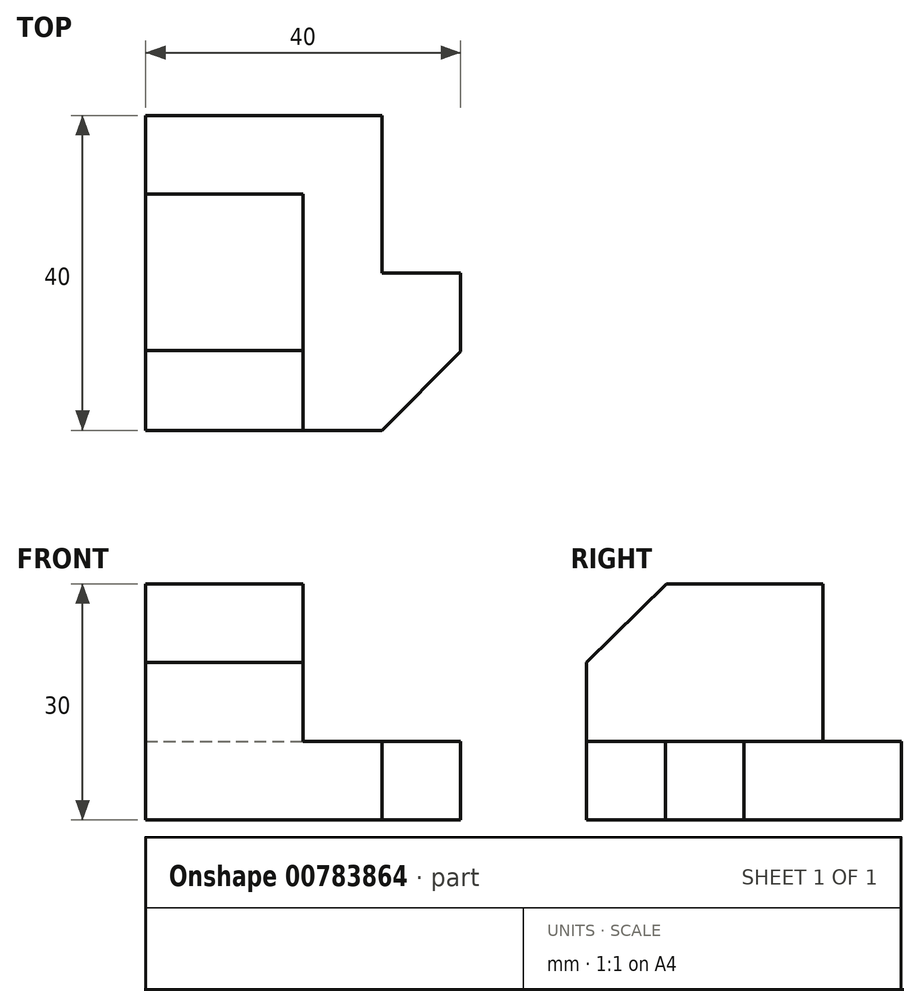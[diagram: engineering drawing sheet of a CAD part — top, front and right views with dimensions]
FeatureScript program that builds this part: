
annotation { "Feature Type Name" : "Feature", "Feature Type Description" : "" }
export const myFeature = defineFeature(function(context is Context, id is Id, definition is map)
    precondition{}
    {
        {
            var Q0;
            Q0=qCreatedBy(makeId("Top.planeOp"),FACE);
            var sketch = newSketch(context, id + "F0", { "sketchPlane" : qUnion([Q0])});
            skLineSegment(sketch, "E0.bottom", {"start": v(0, 0) * mm, "end": v(40, 0) * mm});
            skLineSegment(sketch, "E0.top", {"start": v(0, 40) * mm, "end": v(40, 40) * mm});
            skLineSegment(sketch, "E0.left", {"start": v(0, 0) * mm, "end": v(0, 40) * mm});
            skLineSegment(sketch, "E0.right", {"start": v(40, 0) * mm, "end": v(40, 40) * mm});
            skSolve(sketch);
        }
        {
            var Q0;
            Q0=makeQuery(id+"F0.imprint","IMPRINT",FACE,{"disambiguationData":[TD([[makeQuery(id+"F0.imprint","IMPRINT",EDGE,{"derivedFrom":sQuery(id+"F0.wireOp",EDGE,"E0.bottom")}),1.0]])]});
            extrude(context, id + "F1", {"entities" : qUnion([Q0]), "depth" : 30 * mm, "offsetDistance" : 25 * mm});
        }
        {
            var Q0;
            Q0=makeQuery(id+"F1.opExtrude","CAP_FACE",FACE,{"disambiguationData":[OSD([sQuery(id+"F0.wireOp",EDGE,"E0.bottom"),sQuery(id+"F0.wireOp",EDGE,"E0.top"),sQuery(id+"F0.wireOp",EDGE,"E0.left"),sQuery(id+"F0.wireOp",EDGE,"E0.right")])],"isStart":false});
            var sketch = newSketch(context, id + "F2", { "sketchPlane" : qUnion([Q0])});
            skLineSegment(sketch, "E1.bottom", {"start": v(40, 40) * mm, "end": v(30, 40) * mm});
            skLineSegment(sketch, "E1.top", {"start": v(40, 20) * mm, "end": v(30, 20) * mm});
            skLineSegment(sketch, "E1.left", {"start": v(40, 40) * mm, "end": v(40, 20) * mm});
            skLineSegment(sketch, "E1.right", {"start": v(30, 40) * mm, "end": v(30, 20) * mm});
            skSolve(sketch);
        }
        {
            var Q0;
            Q0=makeQuery(id+"F2.imprint","IMPRINT",FACE,{"disambiguationData":[TD([[makeQuery(id+"F2.imprint","IMPRINT",EDGE,{"derivedFrom":sQuery(id+"F2.wireOp",EDGE,"E1.bottom")}),-1.0]])]});
            extrude(context, id + "F3", {"entities" : qUnion([Q0]), "operationType" : NewBodyOperationType.REMOVE, "oppositeDirection" : true, "depth" : 30 * mm, "offsetDistance" : 25 * mm});
        }
        {
            var Q0;
            Q0=makeQuery(id+"F1.opExtrude","CAP_FACE",FACE,{"disambiguationData":[OSD([sQuery(id+"F0.wireOp",EDGE,"E0.bottom"),sQuery(id+"F0.wireOp",EDGE,"E0.top"),sQuery(id+"F0.wireOp",EDGE,"E0.left"),sQuery(id+"F0.wireOp",EDGE,"E0.right")])],"isStart":false});
            var sketch = newSketch(context, id + "F4", { "sketchPlane" : qUnion([Q0])});
            skLineSegment(sketch, "E2", {"start": v(0, 40) * mm, "end": v(0, 30) * mm});
            skLineSegment(sketch, "E3", {"start": v(0, 30) * mm, "end": v(20, 30) * mm});
            skLineSegment(sketch, "E4", {"start": v(20, 30) * mm, "end": v(20, 0) * mm});
            skLineSegment(sketch, "E5", {"start": v(20, 0) * mm, "end": v(40, 0) * mm});
            skLineSegment(sketch, "E6", {"start": v(40, 0) * mm, "end": v(40, 20) * mm});
            skLineSegment(sketch, "E7", {"start": v(40, 20) * mm, "end": v(30, 20) * mm});
            skLineSegment(sketch, "E8", {"start": v(30, 20) * mm, "end": v(30, 40) * mm});
            skLineSegment(sketch, "E9", {"start": v(30, 40) * mm, "end": v(0, 40) * mm});
            skSolve(sketch);
        }
        {
            var Q0;
            Q0=makeQuery(id+"F4.imprint","IMPRINT",FACE,{"disambiguationData":[TD([[makeQuery(id+"F4.imprint","IMPRINT",EDGE,{"derivedFrom":sQuery(id+"F4.wireOp",EDGE,"E2")}),-1.0]])]});
            extrude(context, id + "F5", {"entities" : qUnion([Q0]), "operationType" : NewBodyOperationType.REMOVE, "oppositeDirection" : true, "depth" : 20 * mm, "offsetDistance" : 25 * mm});
        }
        {
            var Q0;
            Q0=makeQuery(id+"F1.opExtrude","CAP_FACE",FACE,{"disambiguationData":[OSD([sQuery(id+"F0.wireOp",EDGE,"E0.bottom"),sQuery(id+"F0.wireOp",EDGE,"E0.top"),sQuery(id+"F0.wireOp",EDGE,"E0.left"),sQuery(id+"F0.wireOp",EDGE,"E0.right")])],"isStart":false});
            var sketch = newSketch(context, id + "F6", { "sketchPlane" : qUnion([Q0])});
            skLineSegment(sketch, "E10", {"start": v(40.19, 19.93) * mm, "end": v(40.19, 9.93) * mm});
            skLineSegment(sketch, "E11", {"start": v(39.7, 0) * mm, "end": v(29.7, 0) * mm});
            skLineSegment(sketch, "E12", {"start": v(29.7, 0) * mm, "end": v(40.19, 9.93) * mm});
            skSolve(sketch);
        }
        {
            var Q0;
            Q0=makeQuery(id+"F5.boolean.opBoolean","COPY",FACE,{"derivedFrom":makeQuery(id+"F5.opExtrude","CAP_FACE",FACE,{"disambiguationData":[OSD([sQuery(id+"F4.wireOp",EDGE,"E2"),sQuery(id+"F4.wireOp",EDGE,"E3"),sQuery(id+"F4.wireOp",EDGE,"E4"),sQuery(id+"F4.wireOp",EDGE,"E5"),sQuery(id+"F4.wireOp",EDGE,"E6"),sQuery(id+"F4.wireOp",EDGE,"E7"),sQuery(id+"F4.wireOp",EDGE,"E8"),sQuery(id+"F4.wireOp",EDGE,"E9")])],"isStart":false})});
            var sketch = newSketch(context, id + "F7", { "sketchPlane" : qUnion([Q0])});
            skLineSegment(sketch, "E13", {"start": v(40, 10) * mm, "end": v(40, 0) * mm});
            skLineSegment(sketch, "E14", {"start": v(40, 0) * mm, "end": v(30, 0) * mm});
            skLineSegment(sketch, "E15", {"start": v(30, 0) * mm, "end": v(40, 10) * mm});
            skSolve(sketch);
        }
        {
            var Q0;
            Q0=makeQuery(id+"F7.imprint","IMPRINT",FACE,{"disambiguationData":[TD([[makeQuery(id+"F7.imprint","IMPRINT",EDGE,{"derivedFrom":sQuery(id+"F7.wireOp",EDGE,"E13")}),1.0]])]});
            extrude(context, id + "F8", {"entities" : qUnion([Q0]), "operationType" : NewBodyOperationType.REMOVE, "oppositeDirection" : true, "depth" : 10 * mm, "offsetDistance" : 25 * mm});
        }
        {
            var Q0;
            Q0=makeQuery(id+"F1.opExtrude","SWEPT_FACE",FACE,{"disambiguationData":[OSD([sQuery(id+"F0.wireOp",EDGE,"E0.left")])]});
            var sketch = newSketch(context, id + "F9", { "sketchPlane" : qUnion([Q0])});
            skLineSegment(sketch, "E16", {"start": v(0, 30) * mm, "end": v(0, 20) * mm});
            skLineSegment(sketch, "E17", {"start": v(0, 20) * mm, "end": v(-10.13, 30) * mm});
            skLineSegment(sketch, "E18", {"start": v(-10.13, 30) * mm, "end": v(0, 30) * mm});
            skSolve(sketch);
        }
        {
            var Q0;
            Q0=makeQuery(id+"F9.imprint","IMPRINT",FACE,{"disambiguationData":[TD([[makeQuery(id+"F9.imprint","IMPRINT",EDGE,{"derivedFrom":sQuery(id+"F9.wireOp",EDGE,"E16")}),-1.0]])]});
            extrude(context, id + "F10", {"entities" : qUnion([Q0]), "operationType" : NewBodyOperationType.REMOVE, "oppositeDirection" : true, "depth" : 25 * mm, "offsetDistance" : 25 * mm});
        }
    });
